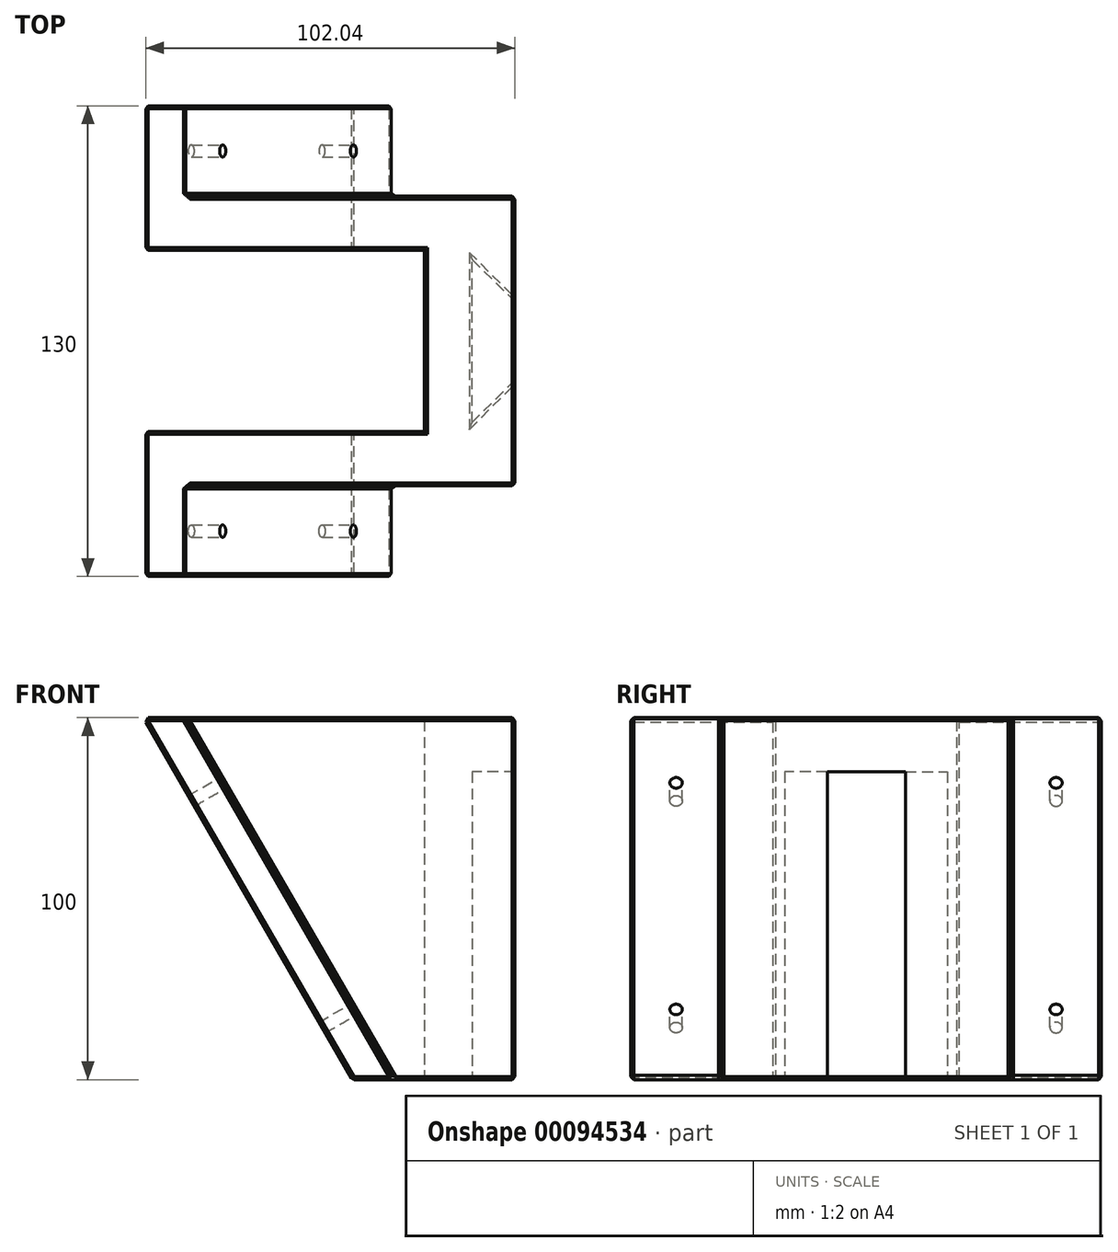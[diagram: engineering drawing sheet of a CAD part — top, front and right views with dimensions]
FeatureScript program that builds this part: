
annotation { "Feature Type Name" : "Feature", "Feature Type Description" : "" }
export const myFeature = defineFeature(function(context is Context, id is Id, definition is map)
    precondition{}
    {
        {
            var Q0;
            Q0=qCreatedBy(makeId("Top.planeOp"),FACE);
            var sketch = newSketch(context, id + "F16", { "sketchPlane" : qUnion([Q0])});
            skLineSegment(sketch, "E0", {"start": v(0, 0) * mm, "end": v(-18.8, 0) * mm});
            skLineSegment(sketch, "E1", {"start": v(-6.25, -9.97) * mm, "end": v(-18.8, -22.5) * mm});
            skLineSegment(sketch, "E2", {"start": v(-18.8, -22.5) * mm, "end": v(-18.8, 22.5) * mm});
            skLineSegment(sketch, "E3", {"start": v(-18.8, 22.5) * mm, "end": v(-6.2, 10.08) * mm});
            skLineSegment(sketch, "E4.bottom", {"start": v(-52, 40) * mm, "end": v(-7, 40) * mm});
            skLineSegment(sketch, "E4.top", {"start": v(-52, -40) * mm, "end": v(-7, -40) * mm});
            skLineSegment(sketch, "E4.right", {"start": v(-7, 40) * mm, "end": v(-7, -40) * mm});
            skPoint(sketch, "E4.middle", {"position": v(-17, 0) * mm});
            skLineSegment(sketch, "E5", {"start": v(-52, 0) * mm, "end": v(-52, 40) * mm});
            skLineSegment(sketch, "E6", {"start": v(-52, 0) * mm, "end": v(-52, -40) * mm});
            skSolve(sketch);
        }
        {
            var Q0;
            {var subQ2=sQuery(id+"F16.wireOp",EDGE,"E2");Q0=makeQuery(id+"F16.imprint","IMPRINT",FACE,{"disambiguationData":[TD([[makeQuery(id+"F16.imprint","IMPRINT",EDGE,{"derivedFrom":subQ2}),1.0]])]});}
            extrude(context, id + "F0", {"entities" : qUnion([Q0]), "depth" : 100 * mm});
        }
        {
            var Q0;
            Q0=makeQuery(id+"F0.opExtrude","SWEPT_FACE",FACE,{"disambiguationData":[OSD([sQuery(id+"F16.wireOp",EDGE,"E4.bottom")])]});
            var sketch = newSketch(context, id + "F1", { "sketchPlane" : qUnion([Q0])});
            skLineSegment(sketch, "E7", {"start": v(52, 100) * mm, "end": v(109.73, 100) * mm});
            skLineSegment(sketch, "E8", {"start": v(109.73, 100) * mm, "end": v(52, 0) * mm});
            skSolve(sketch);
        }
        {
            var Q0;
            Q0=makeQuery(id+"F1.imprint","IMPRINT",FACE,{"disambiguationData":[TD([[makeQuery(id+"F1.imprint","IMPRINT",EDGE,{"derivedFrom":sQuery(id+"F1.wireOp",EDGE,"E7")}),-1.0]])]});
            var Q1;
            Q1=makeQuery(id+"F0.opExtrude","SWEPT_FACE",FACE,{"disambiguationData":[OSD([sQuery(id+"F16.wireOp",EDGE,"E4.top")])]});
            extrude(context, id + "F2", {"entities" : qUnion([Q0]), "operationType" : NewBodyOperationType.ADD, "oppositeDirection" : true, "endBoundEntityFace" : qUnion([Q1]), "depth" : 15 * mm});
        }
        {
            var Q0;
            Q0=makeQuery(id+"F0.opExtrude","SWEPT_FACE",FACE,{"disambiguationData":[OSD([sQuery(id+"F16.wireOp",EDGE,"E4.top")])]});
            var sketch = newSketch(context, id + "F3", { "sketchPlane" : qUnion([Q0])});
            skLineSegment(sketch, "E9.0.0", {"start": v(-52, 100) * mm, "end": v(-109.73, 100) * mm});
            skLineSegment(sketch, "E9.0.1", {"start": v(-109.73, 100) * mm, "end": v(-52, 0) * mm});
            skLineSegment(sketch, "E9.0.2", {"start": v(-52, 0) * mm, "end": v(-52, 100) * mm});
            skSolve(sketch);
        }
        {
            var Q0;
            Q0=qSketchRegion(id+"F3",true);
            var Q1;
            Q1=makeQuery(id+"F3.imprint","IMPRINT",FACE,{"disambiguationData":[TD([[makeQuery(id+"F3.imprint","IMPRINT",EDGE,{"derivedFrom":sQuery(id+"F3.wireOp",EDGE,"E9.0.0")}),1.0]])]});
            extrude(context, id + "F4", {"entities" : qUnion([Q0, Q1]), "operationType" : NewBodyOperationType.ADD, "oppositeDirection" : true, "depth" : 15 * mm});
        }
        {
            var Q0;
            {var subQ0=sQuery(id+"F16.wireOp",EDGE,"E4.bottom");Q0=makeQuery(id+"F2.boolean.opBoolean","MERGE",FACE,{"derivedFrom":[makeQuery(id+"F0.opExtrude","SWEPT_FACE",FACE,{"disambiguationData":[OSD([subQ0])]}),makeQuery(id+"F2.opExtrude","CAP_FACE",FACE,{"disambiguationData":[OSD([subQ0,sQuery(id+"F16.wireOp",EDGE,"E5"),sQuery(id+"F1.wireOp",EDGE,"E7"),sQuery(id+"F1.wireOp",EDGE,"E8")])],"isStart":true})]});}
            var sketch = newSketch(context, id + "F5", { "sketchPlane" : qUnion([Q0])});
            skLineSegment(sketch, "E10.0", {"start": v(103.1, 108.54) * mm, "end": v(30.72, -16.85) * mm});
            skSolve(sketch);
        }
        {
            var Q0;
            {var subQ6=makeQuery(id+"F2.opExtrude","CAP_EDGE",EDGE,{"disambiguationData":[OSD([sQuery(id+"F1.wireOp",EDGE,"E8")])],"isStart":true});Q0=makeQuery(id+"F5.imprint","IMPRINT",FACE,{"disambiguationData":[TD([[makeQuery(id+"F5.imprint","IMPRINT",EDGE,{"derivedFrom":subQ6}),-1.0]])]});}
            extrude(context, id + "F6", {"entities" : qUnion([Q0]), "operationType" : NewBodyOperationType.ADD, "depth" : 25 * mm});
        }
        {
            var Q0;
            Q0=makeQuery(id+"F4.boolean.opBoolean","MERGE",FACE,{"derivedFrom":[makeQuery(id+"F0.opExtrude","SWEPT_FACE",FACE,{"disambiguationData":[OSD([sQuery(id+"F16.wireOp",EDGE,"E4.top")])]}),makeQuery(id+"F4.opExtrude","CAP_FACE",FACE,{"disambiguationData":[OSD([sQuery(id+"F3.wireOp",EDGE,"E9.0.0"),sQuery(id+"F3.wireOp",EDGE,"E9.0.1"),sQuery(id+"F3.wireOp",EDGE,"E9.0.2")])],"isStart":true})]});
            var sketch = newSketch(context, id + "F7", { "sketchPlane" : qUnion([Q0])});
            skLineSegment(sketch, "E11.0", {"start": v(-107.94, 116.9) * mm, "end": v(-29.9, -18.26) * mm});
            skSolve(sketch);
        }
        {
            var Q0;
            {var subQ6=makeQuery(id+"F4.opExtrude","CAP_EDGE",EDGE,{"disambiguationData":[OSD([sQuery(id+"F3.wireOp",EDGE,"E9.0.1")])],"isStart":true});Q0=makeQuery(id+"F7.imprint","IMPRINT",FACE,{"disambiguationData":[TD([[makeQuery(id+"F7.imprint","IMPRINT",EDGE,{"derivedFrom":subQ6}),1.0]])]});}
            extrude(context, id + "F8", {"entities" : qUnion([Q0]), "operationType" : NewBodyOperationType.ADD, "depth" : 25 * mm});
        }
        {
            var Q0;
            {var subQ0=sQuery(id+"F16.wireOp",EDGE,"E2");var subQ1=sQuery(id+"F16.wireOp",EDGE,"E0");var subQ2=makeQuery(id+"F16.imprint","INTERSECT",VERTEX,{"derivedFrom":[subQ1,subQ0]});Q0=makeQuery(id+"F16.imprint","IMPRINT",FACE,{"disambiguationData":[TD([[makeQuery(id+"F16.imprint","IMPRINT",EDGE,{"disambiguationData":[TD([[subQ2,1.0]])],"derivedFrom":subQ1}),1.0]])]});}
            var Q1;
            {var subQ0=sQuery(id+"F16.wireOp",EDGE,"E2");var subQ1=sQuery(id+"F16.wireOp",EDGE,"E0");var subQ2=makeQuery(id+"F16.imprint","INTERSECT",VERTEX,{"derivedFrom":[subQ1,subQ0]});Q1=makeQuery(id+"F16.imprint","IMPRINT",FACE,{"disambiguationData":[TD([[makeQuery(id+"F16.imprint","IMPRINT",EDGE,{"disambiguationData":[TD([[subQ2,1.0]])],"derivedFrom":subQ1}),-1.0]])]});}
            var Q2;
            {var subQ0=sQuery(id+"F3.wireOp",EDGE,"E9.0.0");var subQ1=sQuery(id+"F16.wireOp",EDGE,"E4.top");var subQ2=sQuery(id+"F1.wireOp",EDGE,"E7");var subQ3=sQuery(id+"F16.wireOp",EDGE,"E4.bottom");Q2=makeQuery(id+"F8.boolean.opBoolean","MERGE",FACE,{"derivedFrom":[makeQuery(id+"F6.boolean.opBoolean","MERGE",FACE,{"derivedFrom":[makeQuery(id+"F4.boolean.opBoolean","MERGE",FACE,{"derivedFrom":[makeQuery(id+"F2.boolean.opBoolean","MERGE",FACE,{"derivedFrom":[makeQuery(id+"F0.opExtrude","CAP_FACE",FACE,{"disambiguationData":[OSD([sQuery(id+"F16.wireOp",EDGE,"E1"),sQuery(id+"F16.wireOp",EDGE,"E2"),sQuery(id+"F16.wireOp",EDGE,"E3"),subQ3,subQ1,sQuery(id+"F16.wireOp",EDGE,"E4.right"),sQuery(id+"F16.wireOp",EDGE,"E5"),sQuery(id+"F16.wireOp",EDGE,"E6")])],"isStart":false}),makeQuery(id+"F2.opExtrude","SWEPT_FACE",FACE,{"disambiguationData":[OSD([subQ2])]})]}),makeQuery(id+"F4.opExtrude","SWEPT_FACE",FACE,{"disambiguationData":[OSD([subQ0])]})]}),makeQuery(id+"F6.opExtrude","SWEPT_FACE",FACE,{"disambiguationData":[OSD([subQ3,subQ2])]})]}),makeQuery(id+"F8.opExtrude","SWEPT_FACE",FACE,{"disambiguationData":[OSD([subQ1,subQ0])]})]});}
            extrude(context, id + "F9", {"entities" : qUnion([Q0, Q1]), "operationType" : NewBodyOperationType.ADD, "endBound" : BoundingType.UP_TO_SURFACE, "endBoundEntityFace" : qUnion([Q2]), "depth" : 25 * mm, "hasSecondDirection" : true, "secondDirectionOppositeDirection" : false, "secondDirectionDepth" : 85 * mm});
        }
        {
            var Q0;
            Q0=makeQuery(id+"F0.opExtrude","SWEPT_FACE",FACE,{"disambiguationData":[OSD([sQuery(id+"F16.wireOp",EDGE,"E5"),sQuery(id+"F16.wireOp",EDGE,"E6")])]});
            extrude(context, id + "F10", {"entities" : qUnion([Q0]), "operationType" : NewBodyOperationType.REMOVE, "oppositeDirection" : true, "depth" : 20 * mm});
        }
        {
            var Q0;
            {var subQ0=sQuery(id+"F16.wireOp",EDGE,"E4.right");var subQ1=sQuery(id+"F16.wireOp",EDGE,"E3");var subQ2=sQuery(id+"F16.wireOp",EDGE,"E2");var subQ3=sQuery(id+"F16.wireOp",EDGE,"E1");var subQ4=sQuery(id+"F3.wireOp",EDGE,"E9.0.0");var subQ5=sQuery(id+"F16.wireOp",EDGE,"E4.top");var subQ6=sQuery(id+"F1.wireOp",EDGE,"E7");var subQ7=sQuery(id+"F16.wireOp",EDGE,"E4.bottom");Q0=makeQuery(id+"F9.boolean.opBoolean","MERGE",FACE,{"derivedFrom":[makeQuery(id+"F8.boolean.opBoolean","MERGE",FACE,{"derivedFrom":[makeQuery(id+"F6.boolean.opBoolean","MERGE",FACE,{"derivedFrom":[makeQuery(id+"F4.boolean.opBoolean","MERGE",FACE,{"derivedFrom":[makeQuery(id+"F2.boolean.opBoolean","MERGE",FACE,{"derivedFrom":[makeQuery(id+"F0.opExtrude","CAP_FACE",FACE,{"disambiguationData":[OSD([subQ3,subQ2,subQ1,subQ7,subQ5,subQ0,sQuery(id+"F16.wireOp",EDGE,"E5"),sQuery(id+"F16.wireOp",EDGE,"E6")])],"isStart":false}),makeQuery(id+"F2.opExtrude","SWEPT_FACE",FACE,{"disambiguationData":[OSD([subQ6])]})]}),makeQuery(id+"F4.opExtrude","SWEPT_FACE",FACE,{"disambiguationData":[OSD([subQ4])]})]}),makeQuery(id+"F6.opExtrude","SWEPT_FACE",FACE,{"disambiguationData":[OSD([subQ7,subQ6])]})]}),makeQuery(id+"F8.opExtrude","SWEPT_FACE",FACE,{"disambiguationData":[OSD([subQ5,subQ4])]})]}),makeQuery(id+"F9.opExtrude","CAP_FACE",FACE,{"disambiguationData":[OSD([subQ3,subQ2,subQ1,subQ0])],"isStart":false})]});}
            var Q1;
            Q1=makeQuery(id+"F8.opExtrude","SWEPT_FACE",FACE,{"disambiguationData":[OSD([sQuery(id+"F7.wireOp",EDGE,"E11.0")])]});
            var Q2;
            Q2=makeQuery(id+"F6.opExtrude","SWEPT_FACE",FACE,{"disambiguationData":[OSD([sQuery(id+"F5.wireOp",EDGE,"E10.0")])]});
            var Q3;
            {var subQ0=sQuery(id+"F16.wireOp",EDGE,"E4.bottom");Q3=makeQuery(id+"F2.boolean.opBoolean","MERGE",FACE,{"derivedFrom":[makeQuery(id+"F0.opExtrude","SWEPT_FACE",FACE,{"disambiguationData":[OSD([subQ0])]}),makeQuery(id+"F2.opExtrude","CAP_FACE",FACE,{"disambiguationData":[OSD([subQ0,sQuery(id+"F16.wireOp",EDGE,"E5"),sQuery(id+"F1.wireOp",EDGE,"E7"),sQuery(id+"F1.wireOp",EDGE,"E8")])],"isStart":true})]});}
            var Q4;
            Q4=makeQuery(id+"F4.boolean.opBoolean","MERGE",FACE,{"derivedFrom":[makeQuery(id+"F0.opExtrude","SWEPT_FACE",FACE,{"disambiguationData":[OSD([sQuery(id+"F16.wireOp",EDGE,"E4.top")])]}),makeQuery(id+"F4.opExtrude","CAP_FACE",FACE,{"disambiguationData":[OSD([sQuery(id+"F3.wireOp",EDGE,"E9.0.0"),sQuery(id+"F3.wireOp",EDGE,"E9.0.1"),sQuery(id+"F3.wireOp",EDGE,"E9.0.2")])],"isStart":true})]});
            var Q5;
            {var subQ0=sQuery(id+"F16.wireOp",EDGE,"E4.top");var subQ1=sQuery(id+"F16.wireOp",EDGE,"E4.bottom");Q5=makeQuery(id+"F8.boolean.opBoolean","MERGE",FACE,{"derivedFrom":[makeQuery(id+"F6.boolean.opBoolean","MERGE",FACE,{"derivedFrom":[makeQuery(id+"F0.opExtrude","CAP_FACE",FACE,{"disambiguationData":[OSD([sQuery(id+"F16.wireOp",EDGE,"E1"),sQuery(id+"F16.wireOp",EDGE,"E2"),sQuery(id+"F16.wireOp",EDGE,"E3"),subQ1,subQ0,sQuery(id+"F16.wireOp",EDGE,"E4.right"),sQuery(id+"F16.wireOp",EDGE,"E5"),sQuery(id+"F16.wireOp",EDGE,"E6")])],"isStart":true}),makeQuery(id+"F6.opExtrude","SWEPT_FACE",FACE,{"disambiguationData":[OSD([subQ1])]})]}),makeQuery(id+"F8.opExtrude","SWEPT_FACE",FACE,{"disambiguationData":[OSD([subQ0])]})]});}
            var Q6;
            Q6=makeQuery(id+"F8.opExtrude","CAP_FACE",FACE,{"disambiguationData":[OSD([sQuery(id+"F16.wireOp",EDGE,"E4.top"),sQuery(id+"F3.wireOp",EDGE,"E9.0.0"),sQuery(id+"F3.wireOp",EDGE,"E9.0.1"),sQuery(id+"F7.wireOp",EDGE,"E11.0")])],"isStart":false});
            var Q7;
            Q7=makeQuery(id+"F6.opExtrude","CAP_FACE",FACE,{"disambiguationData":[OSD([sQuery(id+"F16.wireOp",EDGE,"E4.bottom"),sQuery(id+"F1.wireOp",EDGE,"E7"),sQuery(id+"F1.wireOp",EDGE,"E8"),sQuery(id+"F5.wireOp",EDGE,"E10.0")])],"isStart":false});
            var Q8;
            {var subQ0=sQuery(id+"F3.wireOp",EDGE,"E9.0.1");Q8=makeQuery(id+"F8.boolean.opBoolean","MERGE",FACE,{"derivedFrom":[makeQuery(id+"F4.opExtrude","SWEPT_FACE",FACE,{"disambiguationData":[OSD([subQ0])]}),makeQuery(id+"F8.opExtrude","SWEPT_FACE",FACE,{"disambiguationData":[OSD([subQ0])]})]});}
            var Q9;
            {var subQ0=sQuery(id+"F1.wireOp",EDGE,"E8");Q9=makeQuery(id+"F6.boolean.opBoolean","MERGE",FACE,{"derivedFrom":[makeQuery(id+"F2.opExtrude","SWEPT_FACE",FACE,{"disambiguationData":[OSD([subQ0])]}),makeQuery(id+"F6.opExtrude","SWEPT_FACE",FACE,{"disambiguationData":[OSD([subQ0])]})]});}
            chamfer(context, id + "F11", {"entities" : qUnion([Q0, Q1, Q2, Q3, Q4, Q5, Q6, Q7, Q8, Q9]), "width" : 0.8 * mm, "tangentPropagation" : true});
        }
        {
            var Q0;
            Q0=makeQuery(id+"F6.opExtrude","SWEPT_FACE",FACE,{"disambiguationData":[OSD([sQuery(id+"F5.wireOp",EDGE,"E10.0")])]});
            var sketch = newSketch(context, id + "F12", { "sketchPlane" : qUnion([Q0])});
            skLineSegment(sketch, "E12", {"start": v(52.5, 134.9) * mm, "end": v(52.5, 22.62) * mm, "construction": true});
            skLineSegment(sketch, "E13.0", {"start": v(41.39, 42.62) * mm, "end": v(63.61, 42.62) * mm, "construction": true});
            skLineSegment(sketch, "E14.0", {"start": v(63.61, 114.9) * mm, "end": v(41.39, 114.9) * mm, "construction": true});
            skCircle(sketch, "E15", {"center": v(52.5, 42.62) * mm, "radius": 1.7 * mm});
            skCircle(sketch, "E16", {"center": v(52.5, 114.9) * mm, "radius": 1.7 * mm});
            skSolve(sketch);
        }
        {
            var Q0;
            Q0=makeQuery(id+"F12.imprint","IMPRINT",FACE,{"disambiguationData":[TD([[makeQuery(id+"F12.imprint","IMPRINT",EDGE,{"derivedFrom":sQuery(id+"F12.wireOp",EDGE,"E15")}),1.0]])]});
            var Q1;
            Q1=makeQuery(id+"F12.imprint","IMPRINT",FACE,{"disambiguationData":[TD([[makeQuery(id+"F12.imprint","IMPRINT",EDGE,{"derivedFrom":sQuery(id+"F12.wireOp",EDGE,"E16")}),1.0]])]});
            extrude(context, id + "F13", {"entities" : qUnion([Q0, Q1]), "operationType" : NewBodyOperationType.REMOVE, "oppositeDirection" : true, "depth" : 25 * mm});
        }
        {
            var Q0;
            Q0=makeQuery(id+"F8.opExtrude","SWEPT_FACE",FACE,{"disambiguationData":[OSD([sQuery(id+"F7.wireOp",EDGE,"E11.0")])]});
            var sketch = newSketch(context, id + "F14", { "sketchPlane" : qUnion([Q0])});
            skLineSegment(sketch, "E17", {"start": v(-52.5, 22.62) * mm, "end": v(-52.5, 134.9) * mm, "construction": true});
            skLineSegment(sketch, "E18.0", {"start": v(-63.61, 42.62) * mm, "end": v(-41.39, 42.62) * mm, "construction": true});
            skLineSegment(sketch, "E19.0", {"start": v(-41.39, 114.9) * mm, "end": v(-63.61, 114.9) * mm, "construction": true});
            skCircle(sketch, "E20", {"center": v(-52.5, 114.9) * mm, "radius": 1.7 * mm});
            skCircle(sketch, "E21", {"center": v(-52.5, 42.62) * mm, "radius": 1.7 * mm});
            skSolve(sketch);
        }
        {
            var Q0;
            Q0=makeQuery(id+"F14.imprint","IMPRINT",FACE,{"disambiguationData":[TD([[makeQuery(id+"F14.imprint","IMPRINT",EDGE,{"derivedFrom":sQuery(id+"F14.wireOp",EDGE,"E20")}),1.0]])]});
            var Q1;
            Q1=makeQuery(id+"F14.imprint","IMPRINT",FACE,{"disambiguationData":[TD([[makeQuery(id+"F14.imprint","IMPRINT",EDGE,{"derivedFrom":sQuery(id+"F14.wireOp",EDGE,"E21")}),1.0]])]});
            extrude(context, id + "F15", {"entities" : qUnion([Q0, Q1]), "operationType" : NewBodyOperationType.REMOVE, "oppositeDirection" : true, "depth" : 25 * mm});
        }
    });
